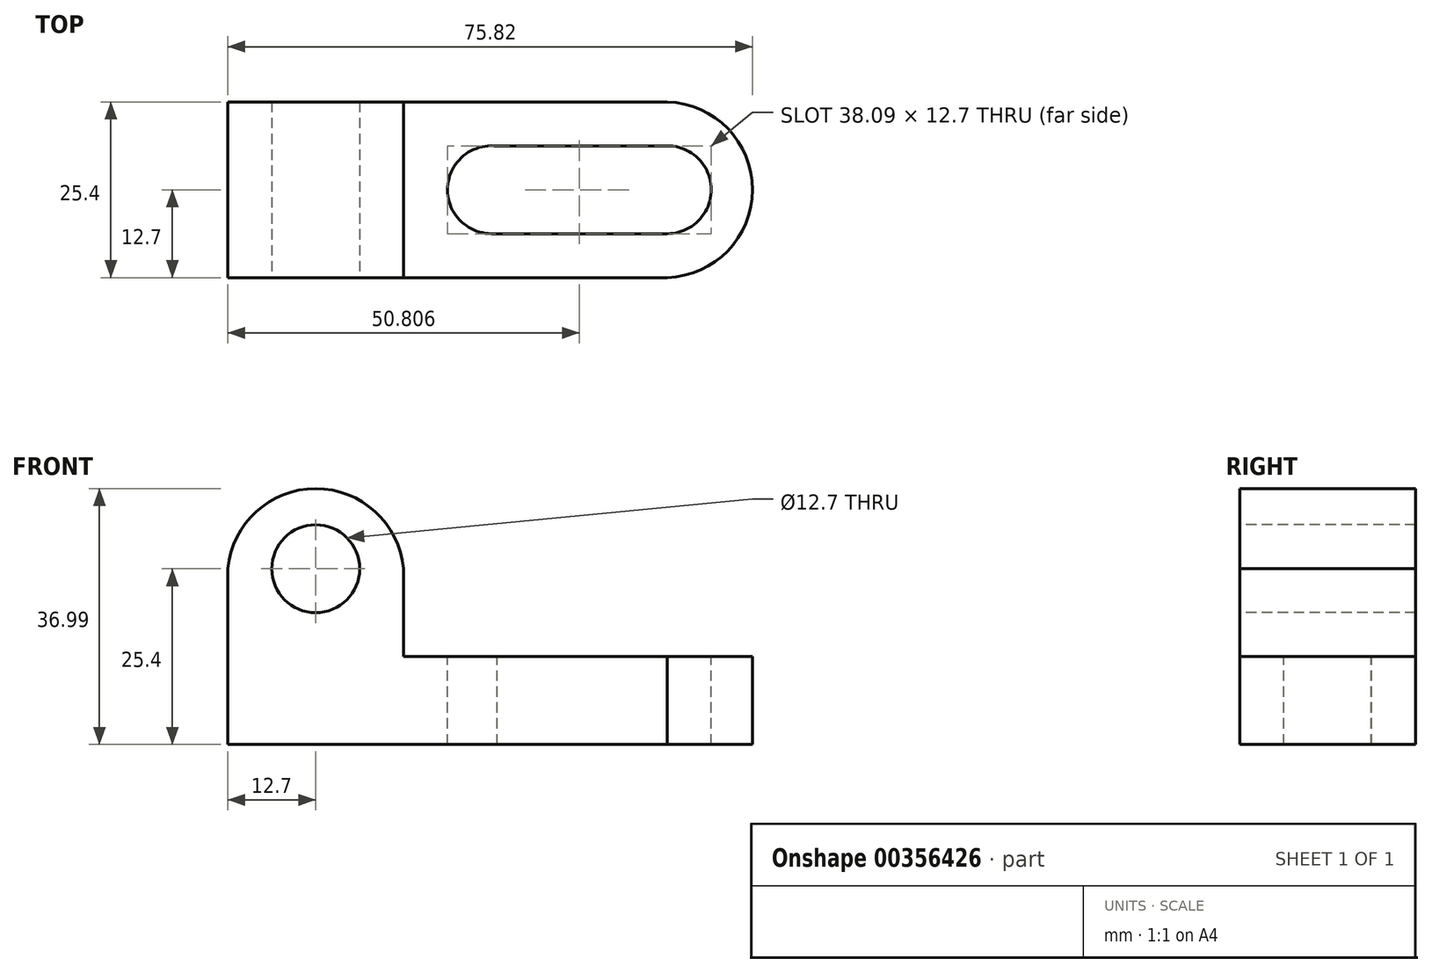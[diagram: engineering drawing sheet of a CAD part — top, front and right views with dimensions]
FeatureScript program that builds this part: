
annotation { "Feature Type Name" : "Feature", "Feature Type Description" : "" }
export const myFeature = defineFeature(function(context is Context, id is Id, definition is map)
    precondition{}
    {
        {
            var Q0;
            Q0=qCreatedBy(makeId("Front.planeOp"),FACE);
            var sketch = newSketch(context, id + "F0", { "sketchPlane" : qUnion([Q0])});
            skLineSegment(sketch, "E0", {"start": v(0, 38.1) * mm, "end": v(0, 0) * mm});
            skLineSegment(sketch, "E1", {"start": v(0, 0) * mm, "end": v(76.2, 0) * mm});
            skLineSegment(sketch, "E2", {"start": v(76.2, 0) * mm, "end": v(76.2, 12.7) * mm});
            skLineSegment(sketch, "E3", {"start": v(76.2, 12.7) * mm, "end": v(25.4, 12.7) * mm});
            skLineSegment(sketch, "E4", {"start": v(25.4, 12.7) * mm, "end": v(25.4, 38.1) * mm});
            skLineSegment(sketch, "E5", {"start": v(25.4, 38.1) * mm, "end": v(0, 38.1) * mm});
            skSolve(sketch);
        }
        {
            var Q0;
            Q0 = qSketchRegion(id + "F0", true);
            extrude(context, id + "F1", {"entities" : qUnion([Q0]), "depth" : 25.4 * mm});
        }
        {
            var Q0;
            Q0=makeQuery(id+"F1.opExtrude","CAP_FACE",FACE,{"disambiguationData":[OSD([sQuery(id+"F0.wireOp",EDGE,"E0"),sQuery(id+"F0.wireOp",EDGE,"E1"),sQuery(id+"F0.wireOp",EDGE,"E2"),sQuery(id+"F0.wireOp",EDGE,"E3"),sQuery(id+"F0.wireOp",EDGE,"E4"),sQuery(id+"F0.wireOp",EDGE,"E5")])],"isStart":false});
            var sketch = newSketch(context, id + "F2", { "sketchPlane" : qUnion([Q0])});
            skCircle(sketch, "E6", {"center": v(12.7, 25.4) * mm, "radius": 6.35 * mm});
            skArc(sketch, "E7", {"start": v(25.4, 25.4) * mm, "mid": v(12.7, 36.99) * mm, "end": v(0, 25.4) * mm});
            skSolve(sketch);
        }
        {
            var Q0;
            Q0=makeQuery(id+"F2.imprint","IMPRINT",FACE,{"disambiguationData":[TD([[makeQuery(id+"F2.imprint","IMPRINT",EDGE,{"derivedFrom":sQuery(id+"F2.wireOp",EDGE,"E6")}),1.0]])]});
            var Q1;
            {var subQ0=sQuery(id+"F2.wireOp",EDGE,"E7");Q1=makeQuery(id+"F2.imprint","IMPRINT",FACE,{"disambiguationData":[TD([[makeQuery(id+"F2.imprint","IMPRINT",EDGE,{"derivedFrom":subQ0}),-1.0]])]});}
            extrude(context, id + "F3", {"entities" : qUnion([Q0, Q1]), "operationType" : NewBodyOperationType.REMOVE, "oppositeDirection" : true, "depth" : 25.4 * mm});
        }
        {
            var Q0;
            Q0=makeQuery(id+"F1.opExtrude","SWEPT_FACE",FACE,{"disambiguationData":[OSD([sQuery(id+"F0.wireOp",EDGE,"E3")])]});
            var sketch = newSketch(context, id + "F4", { "sketchPlane" : qUnion([Q0])});
            skCircle(sketch, "E8", {"center": v(38.1, -12.7) * mm, "radius": 6.35 * mm});
            skCircle(sketch, "E9", {"center": v(63.5, -12.7) * mm, "radius": 6.35 * mm});
            skLineSegment(sketch, "E10", {"start": v(37.28, -6.4) * mm, "end": v(63.49, -6.35) * mm});
            skLineSegment(sketch, "E11", {"start": v(63.49, -6.35) * mm, "end": v(63.5, -19.05) * mm});
            skLineSegment(sketch, "E12", {"start": v(63.5, -19.05) * mm, "end": v(38.1, -19.05) * mm});
            skLineSegment(sketch, "E13", {"start": v(38.1, -19.05) * mm, "end": v(37.28, -6.4) * mm});
            skSolve(sketch);
        }
        {
            var Q0;
            {var subQ0=sQuery(id+"F4.wireOp",EDGE,"E10");var subQ1=sQuery(id+"F4.wireOp",EDGE,"E8");var subQ3=makeQuery(id+"F4.imprint","INTERSECT",VERTEX,{"derivedFrom":[subQ1,subQ0]});Q0=makeQuery(id+"F4.imprint","IMPRINT",FACE,{"disambiguationData":[TD([[makeQuery(id+"F4.imprint","IMPRINT",EDGE,{"disambiguationData":[TD([[subQ3,-1.0]])],"derivedFrom":subQ1}),1.0]])]});}
            var Q1;
            {var subQ0=sQuery(id+"F4.wireOp",EDGE,"E11");Q1=makeQuery(id+"F4.imprint","IMPRINT",FACE,{"disambiguationData":[TD([[makeQuery(id+"F4.imprint","IMPRINT",EDGE,{"derivedFrom":subQ0}),-1.0]])]});}
            var Q2;
            {var subQ0=sQuery(id+"F4.wireOp",EDGE,"E11");Q2=makeQuery(id+"F4.imprint","IMPRINT",FACE,{"disambiguationData":[TD([[makeQuery(id+"F4.imprint","IMPRINT",EDGE,{"derivedFrom":subQ0}),1.0]])]});}
            var Q3;
            {var subQ0=sQuery(id+"F4.wireOp",EDGE,"E12");Q3=makeQuery(id+"F4.imprint","IMPRINT",FACE,{"disambiguationData":[TD([[makeQuery(id+"F4.imprint","IMPRINT",EDGE,{"derivedFrom":subQ0}),-1.0]])]});}
            var Q4;
            {var subQ0=sQuery(id+"F4.wireOp",EDGE,"E13");Q4=makeQuery(id+"F4.imprint","IMPRINT",FACE,{"disambiguationData":[TD([[makeQuery(id+"F4.imprint","IMPRINT",EDGE,{"derivedFrom":subQ0}),-1.0]])]});}
            var Q5;
            {var subQ0=sQuery(id+"F4.wireOp",EDGE,"E13");Q5=makeQuery(id+"F4.imprint","IMPRINT",FACE,{"disambiguationData":[TD([[makeQuery(id+"F4.imprint","IMPRINT",EDGE,{"derivedFrom":subQ0}),1.0]])]});}
            extrude(context, id + "F5", {"entities" : qUnion([Q0, Q1, Q2, Q3, Q4, Q5]), "operationType" : NewBodyOperationType.REMOVE, "oppositeDirection" : true, "depth" : 25.4 * mm});
        }
        {
            var Q0;
            Q0=makeQuery(id+"F1.opExtrude","SWEPT_FACE",FACE,{"disambiguationData":[OSD([sQuery(id+"F0.wireOp",EDGE,"E3")])]});
            var sketch = newSketch(context, id + "F6", { "sketchPlane" : qUnion([Q0])});
            skPoint(sketch, "E14.startSnap0", {"position": v(69.85, -12.7) * mm});
            skArc(sketch, "E15", {"start": v(63.5, -25.4) * mm, "mid": v(75.82, -12.7) * mm, "end": v(63.5, 0) * mm});
            skSolve(sketch);
        }
        {
            var Q0;
            Q0 = qSketchRegion(id + "F6", true);
            var Q1;
            {var subQ0=sQuery(id+"F6.wireOp",EDGE,"E15");Q1=makeQuery(id+"F6.imprint","IMPRINT",FACE,{"disambiguationData":[TD([[makeQuery(id+"F6.imprint","IMPRINT",EDGE,{"derivedFrom":subQ0}),-1.0]])]});}
            extrude(context, id + "F7", {"entities" : qUnion([Q0, Q1]), "operationType" : NewBodyOperationType.REMOVE, "oppositeDirection" : true, "depth" : 25.4 * mm});
        }
    });
